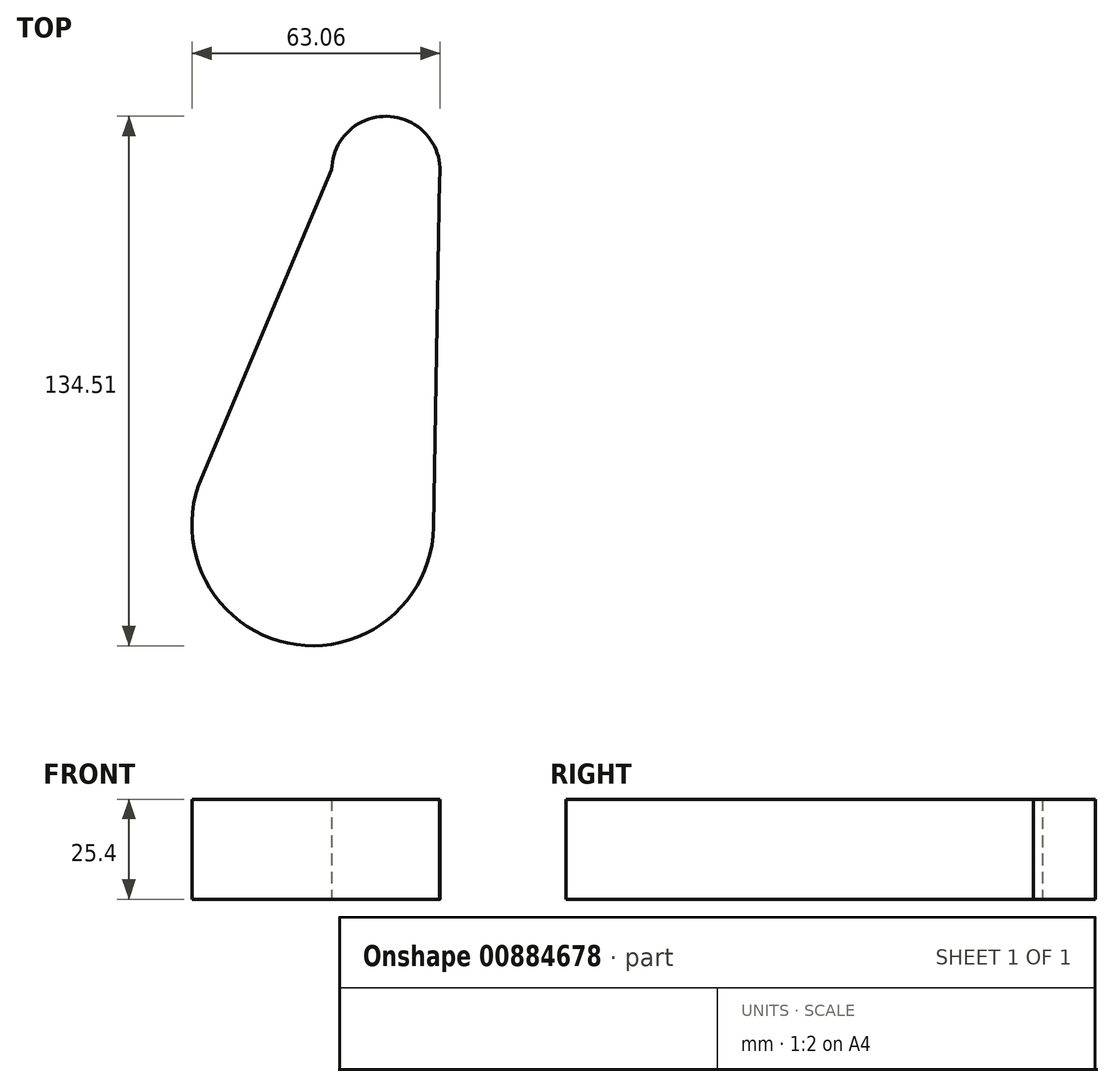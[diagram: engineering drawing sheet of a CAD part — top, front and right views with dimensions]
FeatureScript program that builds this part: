
annotation { "Feature Type Name" : "Feature", "Feature Type Description" : "" }
export const myFeature = defineFeature(function(context is Context, id is Id, definition is map)
    precondition{}
    {
        {
            var Q0;
            Q0=qCreatedBy(makeId("Top.planeOp"),FACE);
            var sketch = newSketch(context, id + "F0", { "sketchPlane" : qUnion([Q0])});
            skCircle(sketch, "E0", {"center": v(44.66, 34.83) * mm, "radius": 13.77 * mm});
            skCircle(sketch, "E1", {"center": v(26.07, -55.2) * mm, "radius": 30.7 * mm});
            skLineSegment(sketch, "E2", {"start": v(58.27, 32.78) * mm, "end": v(56.76, -55.73) * mm});
            skLineSegment(sketch, "E3", {"start": v(30.89, 35.06) * mm, "end": v(-2.21, -43.25) * mm});
            skSolve(sketch);
        }
        {
            var Q0;
            Q0 = qSketchRegion(id + "F0", true);
            var Q1;
            {var subQ0=sQuery(id+"F0.wireOp",EDGE,"E2");Q1=makeQuery(id+"F0.imprint","IMPRINT",FACE,{"disambiguationData":[TD([[makeQuery(id+"F0.imprint","IMPRINT",EDGE,{"derivedFrom":subQ0}),-1.0]])]});}
            var Q2;
            {var subQ0=sQuery(id+"F0.wireOp",EDGE,"E1");var subQ1=makeQuery(id+"F0.imprint","INTERSECT",VERTEX,{"derivedFrom":[subQ0,sQuery(id+"F0.wireOp",EDGE,"E2")]});Q2=makeQuery(id+"F0.imprint","IMPRINT",FACE,{"disambiguationData":[TD([[makeQuery(id+"F0.imprint","IMPRINT",EDGE,{"disambiguationData":[TD([[subQ1,1.0]])],"derivedFrom":subQ0}),1.0]])]});}
            extrude(context, id + "F1", {"entities" : qUnion([Q0, Q1, Q2]), "depth" : 25.4 * mm, "offsetDistance" : 25.4 * mm});
        }
    });
